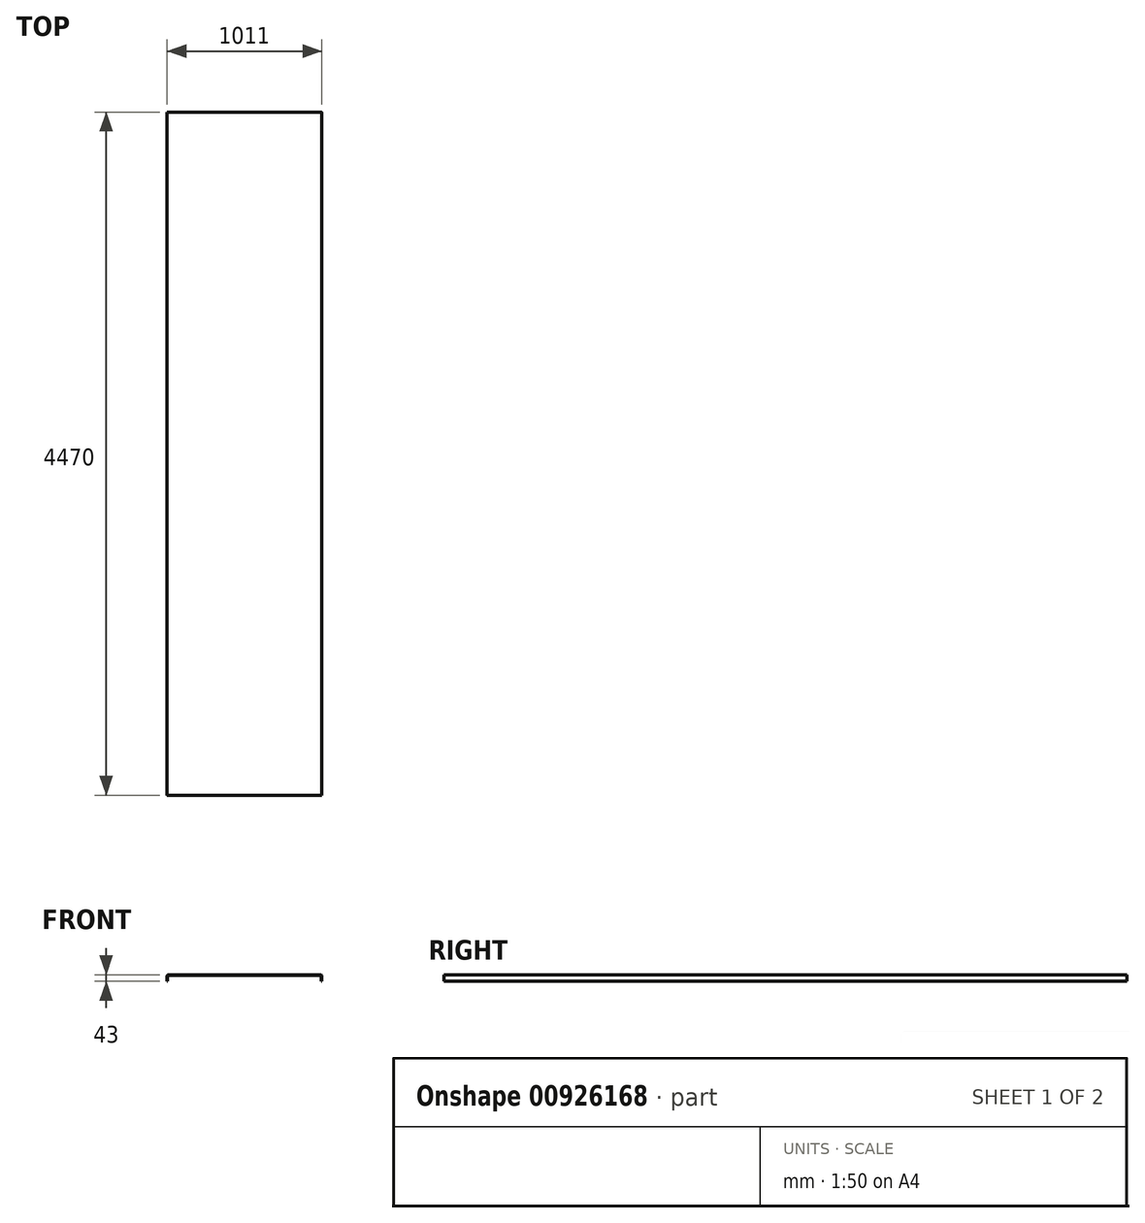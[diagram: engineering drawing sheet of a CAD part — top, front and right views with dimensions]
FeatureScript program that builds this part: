
annotation { "Feature Type Name" : "Feature", "Feature Type Description" : "" }
export const myFeature = defineFeature(function(context is Context, id is Id, definition is map)
    precondition{}
    {
        {
            var Q0;
            Q0=qCreatedBy(makeId("Front.planeOp"),FACE);
            var sketch = newSketch(context, id + "F0", { "sketchPlane" : qUnion([Q0])});
            skLineSegment(sketch, "E0", {"start": v(0, 0) * mm, "end": v(0, 37) * mm});
            skLineSegment(sketch, "E1", {"start": v(6, 43) * mm, "end": v(1005, 43) * mm});
            skLineSegment(sketch, "E2", {"start": v(1011, 37) * mm, "end": v(1011, 0) * mm});
            skLineSegment(sketch, "E3", {"start": v(1011, 0) * mm, "end": v(1008, 0) * mm});
            skLineSegment(sketch, "E4", {"start": v(1008, 0) * mm, "end": v(1008, 37) * mm});
            skLineSegment(sketch, "E5", {"start": v(1005, 40) * mm, "end": v(6, 40) * mm});
            skLineSegment(sketch, "E6", {"start": v(3, 37) * mm, "end": v(3, 0) * mm});
            skLineSegment(sketch, "E7", {"start": v(3, 0) * mm, "end": v(0, 0) * mm});
            skPoint(sketch, "E8.visualSharp", {"position": v(3, 40) * mm});
            skArc(sketch, "E8.filletArc", {"start": v(6, 40) * mm, "mid": v(3.88, 39.12) * mm, "end": v(3, 37) * mm});
            skPoint(sketch, "E9.visualSharp", {"position": v(0, 43) * mm});
            skArc(sketch, "E9.filletArc", {"start": v(6, 43) * mm, "mid": v(1.76, 41.24) * mm, "end": v(0, 37) * mm});
            skPoint(sketch, "E10.visualSharp", {"position": v(1011, 43) * mm});
            skArc(sketch, "E10.filletArc", {"start": v(1011, 37) * mm, "mid": v(1009.24, 41.24) * mm, "end": v(1005, 43) * mm});
            skPoint(sketch, "E11.visualSharp", {"position": v(1008, 40) * mm});
            skArc(sketch, "E11.filletArc", {"start": v(1008, 37) * mm, "mid": v(1007.12, 39.12) * mm, "end": v(1005, 40) * mm});
            skSolve(sketch);
        }
        {
            var Q0;
            Q0=makeQuery(id+"F0.imprint","IMPRINT",FACE,{"disambiguationData":[TD([[makeQuery(id+"F0.imprint","IMPRINT",EDGE,{"derivedFrom":sQuery(id+"F0.wireOp",EDGE,"E0")}),-1.0]])]});
            extrude(context, id + "F1", {"entities" : qUnion([Q0]), "depth" : 4470 * mm, "offsetDistance" : 25 * mm});
        }
    });
